# Revit family: Haworth_LC10P_Table
name_source: partatom
category: Furniture
revit_build: Autodesk Revit 2018 (Build: 20170223_1515(x64)
units: mm (PartAtom-declared; Revit-internal decimal feet)

## family parameters
Always vertical = Yes
Cut with Voids When Loaded = No
OmniClass Number = 23.40.70.14.64.21
OmniClass Title = Systems Furniture
Room Calculation Point = No
Shared = No
Work Plane-Based = No

## types (5) — shared parameters
Assembly Code = E2020200
Description = Haworth LC10P Table
Frame Height = 1 5/16"
Frame Offset = 3/16"
Glide Height = 5/16"
Hardware Finish = Haworth _ Paint _ Collection Black
Leg Finish = Haworth _ Metal _ Chrome
Leg Half = 1"
Manufacturer = Haworth
Model = HCCS-L10
Revision Number = 4
Size = Verify Final Dim. w/ Haworth
Support Location Offset = 3/8"
Support Location_Front_Back = 1 3/4"
Support Location_Side = 1 3/4"
Table Top Thickness = 9/16"
URL = http://www.haworth.com
URL - Product = https://www.haworth.com
Warranty = http://www.haworth.com

## per-type parameters (varying)
| type | Actual Depth | Actual Height | Actual Width | High Table_Large Square | High Table_Rectangle | Low Table_Large Square | Low Table_Rectangle | Low Table_Small Square |
| HCCS-L10 - High Table Large Square | 55" | 27 1/2" | 55" | Yes | No | No | No | No |
| HCCS-L10 - High Table Rectangle | 31 1/2" | 27 1/2" | 47" | No | Yes | No | No | No |
| HCCS-L10 - Low Table Large Square | 55" | 13" | 55" | No | No | Yes | No | No |
| HCCS-L10 - Low Table Rectangle | 31 1/2" | 13" | 47" | No | No | No | Yes | No |
| HCCS-L10 - Low Table Small Square | 27 1/2" | 13" | 27 1/2" | No | No | No | No | Yes |

## geometry (parser evidence)
native form markers: Sweep x2
no freeform markers — native parametric forms only
